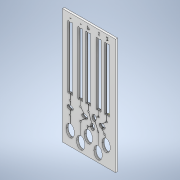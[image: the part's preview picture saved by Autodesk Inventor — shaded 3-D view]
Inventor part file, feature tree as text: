
AUTODESK INVENTOR PART (.ipt)
format: ipt  version: 2021 (Build 250183000, 183)  size: 674,304 bytes
history: mixed  units: in
note: dims shown in document units (in); Inventor stores cm internally (conversion verified against a paired STEP export)
features: sketch x3, extrude x2, other x2, imported_body x1
ambient origin geometry x8: Origin, YZ Plane, XZ Plane, XY Plane, X Axis, Y Axis, Z Axis, Center Point
bodies: 实体1 (imported_parasolid)
feature tree (8):
  sketch  "草图3"  dims[d36=0.0787in d37=0.0in d44=0.0787in d45=0.0in]
  extrude  "拉伸2"  Depth=0.0787in TaperAngle=0.0deg
  extrude  "拉伸3"  Depth=0.0344in
  other  "图像2"
  sketch  "草图4"  dims[d38=0.0197in d39=0.0344in]
  sketch  "草图5"  dims[d40=0.0197in d41=0.0344in]
  other  "Cut-Extrude2[1]"
  imported_body  NMx_Import_Brep_tag  [imported B-rep: ~8 faces, bbox_mm=None]
